# Revit family: IEK_Держатель проводника круглого_6-10мм_38мм_Пластик серый
name_source: partatom
category: Обобщенные модели
units: mm (PartAtom-declared; Revit-internal decimal feet)

## family parameters
Может служить основой для арматурных стержней = Нет
Общий = Да
Основа = Грань
При загрузке вырезать с полостями = Нет
Размер круглого соединителя = Использовать диаметр
Тип детали = Нормальный
Точка расчета площади = Нет

## types (2) — shared parameters
ADSK_URL страницы изделия = https://www.iek.ru
ADSK_Версия Revit = 2019
ADSK_Версия семейства = 1.0
ADSK_Группирование = VIII. ЭЛЕМЕНТЫ ВНЕШНЕЙ МОЛНИЕЗАЩИТЫ
ADSK_Единица измерения = шт
ADSK_Завод-изготовитель = IEK
IEK_URL = https://www.iek.ru
IEK_Описание = Универсальная конструкция держателя позволяет использовать его с проводниками различной формы и габаритами.
zero-valued in all types: Отметка по умолчанию

## per-type parameters (varying)
| type | ADSK_Код изделия | ADSK_Масса | ADSK_Материал | ADSK_Материал наименование | ADSK_Наименование | IEK_Цена за единицу | KSI_CMa_Строительные материалы |
| 8-10мм_Оцинкованная сталь | ZDP80-11-3-18 | 0.089 | Сталь оцинкованная | Сталь оцинкованная | Дер. пров. кругл. 8-10мм бетонный фасад оц. сталь IEK | 470 | 24.10.35.000.08.3.05.06-0001 |
| 8-10мм_Медь | ZDP80-60-1-68-038 | 0.2 | RAL 7024 Графитовый серый | Пластик | Дер. пров. кругл. 6-10мм h=38мм пластик серый IEK | 100 | 01.7.14.03 |
